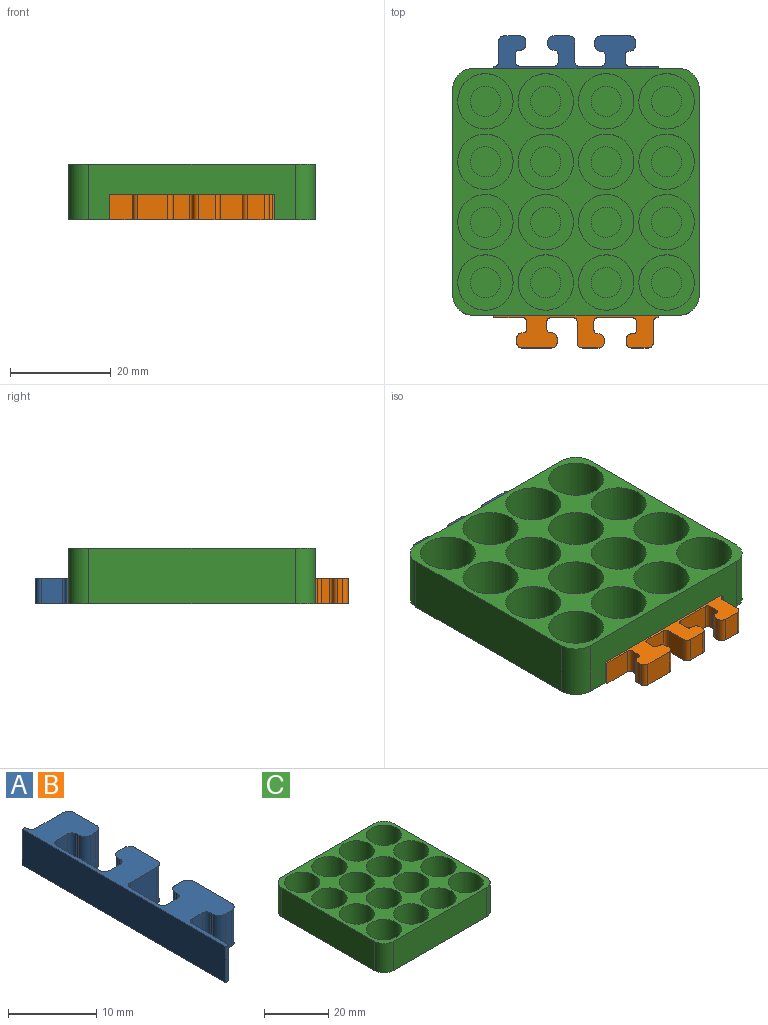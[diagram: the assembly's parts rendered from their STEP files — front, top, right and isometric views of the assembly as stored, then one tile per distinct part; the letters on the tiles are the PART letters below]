
ASSEMBLY  parts=3 mates=2
PART A: 46 faces, bbox 6.5x32.7x5 mm
  f0: plane 5x1.6mm, normal (0,1,0), area 8mm2, adj f24,f25,f38,f39
  f1: plane 5x4.57mm, normal (1,0,0), area 22.9mm2, adj f24,f25,f39,f43
  f2: plane 5x4.3mm, normal (0,-1,0), area 21.5mm2, adj f24,f25,f33,f43
  f3: plane 5x3.37mm, normal (1,0,0), area 16.9mm2, adj f24,f25,f33,f34
  f4: plane 5x0.8mm, normal (0,1,0), area 4mm2, adj f24,f25,f34,f35
  f5: plane 5x0.3mm, normal (-1,0,0), area 1.5mm2, adj f24,f25,f35,f45
  f6: plane 5x1.8mm, normal (0,1,0), area 9mm2, adj f24,f25,f44,f45
  f7: plane 7x5mm, normal (1,0,0), area 35mm2, adj f24,f25,f40,f44
  f8: plane 5x1.8mm, normal (0,-1,0), area 9mm2, adj f24,f25,f40,f41
  f9: plane 5x0.3mm, normal (-1,0,0), area 1.5mm2, adj f24,f25,f30,f41
  f10: plane 5x0.8mm, normal (0,-1,0), area 4mm2, adj f24,f25,f30,f31
  f11: plane 5x3.37mm, normal (1,0,0), area 16.9mm2, adj f24,f25,f31,f32
  f12: plane 5x4.3mm, normal (0,1,0), area 21.5mm2, adj f24,f25,f32,f42
  f13: plane 5x0.3mm, normal (1,0,0), area 1.5mm2, adj f14,f24,f25,f42
  f14: plane 5x0.5mm, normal (0,1,0), area 2.5mm2, adj f13,f15,f24,f25
  f15: plane 32.7x5mm, normal (-1,0,0), area 163.5mm2, adj f14,f16,f24,f25
  f16: plane 5x0.5mm, normal (0,-1,0), area 2.5mm2, adj f15,f17,f24,f25
  f17: plane 5.87x5mm, normal (1,0,0), area 29.4mm2, adj f16,f24,f25,f36
  f18: plane 5x1.6mm, normal (0,-1,0), area 8mm2, adj f24,f25,f36,f37
  f19: plane 5x0.3mm, normal (-1,0,0), area 1.5mm2, adj f24,f25,f26,f37
  f20: plane 5x1mm, normal (0,-1,0), area 5mm2, adj f24,f25,f26,f27
  f21: plane 6x5mm, normal (1,0,0), area 30mm2, adj f24,f25,f27,f28
  f22: plane 5x1mm, normal (0,1,0), area 5mm2, adj f24,f25,f28,f29
  f23: plane 5x0.3mm, normal (-1,0,0), area 1.5mm2, adj f24,f25,f29,f38
  f24: plane 32.7x6.5mm, normal (0,0,1), area 102.9mm2, adj f0,f1,f2,f3,f4,f5,f6,f7
  f25: plane 32.7x6.5mm, normal (0,0,-1), area 102.9mm2, adj f0,f1,f2,f3,f4,f5,f6,f7
  f26: cylinder r=1mm len=5mm, axis (0,0,-1), area 7.9mm2, adj f19,f20,f24,f25
  f27: cylinder r=1mm len=5mm, axis (0,0,-1), area 7.9mm2, adj f20,f21,f24,f25
  f28: cylinder r=1mm len=5mm, axis (0,0,-1), area 7.9mm2, adj f21,f22,f24,f25
  f29: cylinder r=1mm len=5mm, axis (0,0,-1), area 7.9mm2, adj f22,f23,f24,f25
  f30: cylinder r=1mm len=5mm, axis (0,0,-1), area 7.9mm2, adj f9,f10,f24,f25
  f31: cylinder r=1mm len=5mm, axis (0,0,-1), area 7.9mm2, adj f10,f11,f24,f25
  f32: cylinder r=1mm len=5mm, axis (0,0,-1), area 7.9mm2, adj f11,f12,f24,f25
  f33: cylinder r=1mm len=5mm, axis (0,0,-1), area 7.9mm2, adj f2,f3,f24,f25
  f34: cylinder r=1mm len=5mm, axis (0,0,-1), area 7.9mm2, adj f3,f4,f24,f25
  f35: cylinder r=1mm len=5mm, axis (0,0,-1), area 7.9mm2, adj f4,f5,f24,f25
  f36: cylinder r=0.7mm len=5mm, axis (0,0,-1), area 5.5mm2, adj f17,f18,f24,f25
  f37: cylinder r=0.7mm len=5mm, axis (0,0,1), area 5.5mm2, adj f18,f19,f24,f25
  f38: cylinder r=0.7mm len=5mm, axis (0,0,1), area 5.5mm2, adj f0,f23,f24,f25
  f39: cylinder r=0.7mm len=5mm, axis (0,0,-1), area 5.5mm2, adj f0,f1,f24,f25
  f40: cylinder r=0.7mm len=5mm, axis (0,0,-1), area 5.5mm2, adj f7,f8,f24,f25
  f41: cylinder r=0.7mm len=5mm, axis (0,0,1), area 5.5mm2, adj f8,f9,f24,f25
  f42: cylinder r=0.7mm len=5mm, axis (0,0,-1), area 5.5mm2, adj f12,f13,f24,f25
  f43: cylinder r=0.7mm len=5mm, axis (0,0,1), area 5.5mm2, adj f1,f2,f24,f25
  f44: cylinder r=0.7mm len=5mm, axis (0,0,1), area 5.5mm2, adj f6,f7,f24,f25
  f45: cylinder r=0.7mm len=5mm, axis (0,0,1), area 5.5mm2, adj f5,f6,f24,f25
PART B: same geometry as A
PART C: 74 faces, bbox 49x49x11.1 mm
  f0: plane 41x11.1mm, normal (-1,0,0), area 455.1mm2, adj f4,f21,f70,f73
  f1: plane 41x11.1mm, normal (0,-1,0), area 455.1mm2, adj f4,f21,f70,f71
  f2: plane 41x11.1mm, normal (1,0,0), area 455.1mm2, adj f4,f21,f71,f72
  f3: plane 41x11.1mm, normal (0,1,0), area 455.1mm2, adj f4,f21,f72,f73
  f4: plane 49x49mm, normal (0,0,-1), area 2387.3mm2, adj f0,f1,f2,f3,f70,f71,f72,f73
  f5: cylinder r=5.5mm len=11mm, axis (0,0,-1), area 293.7mm2, adj f21,f65
  f6: cylinder r=5.5mm len=11mm, axis (0,0,-1), area 293.7mm2, adj f21,f62
  f7: cylinder r=5.5mm len=11mm, axis (0,0,-1), area 293.7mm2, adj f21,f59
  f8: cylinder r=5.5mm len=11mm, axis (0,0,-1), area 293.7mm2, adj f21,f56
  f9: cylinder r=5.5mm len=11mm, axis (0,0,-1), area 293.7mm2, adj f21,f53
  f10: cylinder r=5.5mm len=11mm, axis (0,0,-1), area 293.7mm2, adj f21,f50
  f11: cylinder r=5.5mm len=11mm, axis (0,0,-1), area 293.7mm2, adj f21,f47
  f12: cylinder r=5.5mm len=11mm, axis (0,0,-1), area 293.7mm2, adj f21,f44
  f13: cylinder r=5.5mm len=11mm, axis (0,0,-1), area 293.7mm2, adj f21,f41
  f14: cylinder r=5.5mm len=11mm, axis (0,0,-1), area 293.7mm2, adj f21,f38
  f15: cylinder r=5.5mm len=11mm, axis (0,0,-1), area 293.7mm2, adj f21,f35
  f16: cylinder r=5.5mm len=11mm, axis (0,0,-1), area 293.7mm2, adj f21,f32
  f17: cylinder r=5.5mm len=11mm, axis (0,0,-1), area 293.7mm2, adj f21,f29
  f18: cylinder r=5.5mm len=11mm, axis (0,0,-1), area 293.7mm2, adj f21,f26
  f19: cylinder r=5.5mm len=11mm, axis (0,0,-1), area 293.7mm2, adj f21,f23
  f20: cylinder r=5.5mm len=11mm, axis (0,0,-1), area 293.7mm2, adj f21,f68
  f21: plane 49x49mm, normal (0,0,1), area 866.7mm2, adj f0,f1,f2,f3,f5,f6,f7,f8
  f22: cylinder r=3mm len=6mm, axis (0,0,-1), area 28.3mm2, adj f23,f24
  f23: plane 11x11mm, normal (0,0,1), area 66.8mm2, adj f19,f22
  f24: plane 6x6mm, normal (0,0,1), area 28.3mm2, adj f22
  f25: cylinder r=3mm len=6mm, axis (0,0,-1), area 28.3mm2, adj f26,f27
  f26: plane 11x11mm, normal (0,0,1), area 66.8mm2, adj f18,f25
  f27: plane 6x6mm, normal (0,0,1), area 28.3mm2, adj f25
  f28: cylinder r=3mm len=6mm, axis (0,0,-1), area 28.3mm2, adj f29,f30
  f29: plane 11x11mm, normal (0,0,1), area 66.8mm2, adj f17,f28
  f30: plane 6x6mm, normal (0,0,1), area 28.3mm2, adj f28
  f31: cylinder r=3mm len=6mm, axis (0,0,-1), area 28.3mm2, adj f32,f33
  f32: plane 11x11mm, normal (0,0,1), area 66.8mm2, adj f16,f31
  f33: plane 6x6mm, normal (0,0,1), area 28.3mm2, adj f31
  f34: cylinder r=3mm len=6mm, axis (0,0,-1), area 28.3mm2, adj f35,f36
  f35: plane 11x11mm, normal (0,0,1), area 66.8mm2, adj f15,f34
  f36: plane 6x6mm, normal (0,0,1), area 28.3mm2, adj f34
  f37: cylinder r=3mm len=6mm, axis (0,0,-1), area 28.3mm2, adj f38,f39
  f38: plane 11x11mm, normal (0,0,1), area 66.8mm2, adj f14,f37
  f39: plane 6x6mm, normal (0,0,1), area 28.3mm2, adj f37
  f40: cylinder r=3mm len=6mm, axis (0,0,-1), area 28.3mm2, adj f41,f42
  f41: plane 11x11mm, normal (0,0,1), area 66.8mm2, adj f13,f40
  f42: plane 6x6mm, normal (0,0,1), area 28.3mm2, adj f40
  f43: cylinder r=3mm len=6mm, axis (0,0,-1), area 28.3mm2, adj f44,f45
  f44: plane 11x11mm, normal (0,0,1), area 66.8mm2, adj f12,f43
  f45: plane 6x6mm, normal (0,0,1), area 28.3mm2, adj f43
  f46: cylinder r=3mm len=6mm, axis (0,0,-1), area 28.3mm2, adj f47,f48
  f47: plane 11x11mm, normal (0,0,1), area 66.8mm2, adj f11,f46
  f48: plane 6x6mm, normal (0,0,1), area 28.3mm2, adj f46
  f49: cylinder r=3mm len=6mm, axis (0,0,-1), area 28.3mm2, adj f50,f51
  f50: plane 11x11mm, normal (0,0,1), area 66.8mm2, adj f10,f49
  f51: plane 6x6mm, normal (0,0,1), area 28.3mm2, adj f49
  f52: cylinder r=3mm len=6mm, axis (0,0,-1), area 28.3mm2, adj f53,f54
  f53: plane 11x11mm, normal (0,0,1), area 66.8mm2, adj f9,f52
  f54: plane 6x6mm, normal (0,0,1), area 28.3mm2, adj f52
  f55: cylinder r=3mm len=6mm, axis (0,0,-1), area 28.3mm2, adj f56,f57
  f56: plane 11x11mm, normal (0,0,1), area 66.8mm2, adj f8,f55
  f57: plane 6x6mm, normal (0,0,1), area 28.3mm2, adj f55
  f58: cylinder r=3mm len=6mm, axis (0,0,-1), area 28.3mm2, adj f59,f60
  f59: plane 11x11mm, normal (0,0,1), area 66.8mm2, adj f7,f58
  f60: plane 6x6mm, normal (0,0,1), area 28.3mm2, adj f58
  f61: cylinder r=3mm len=6mm, axis (0,0,-1), area 28.3mm2, adj f62,f63
  f62: plane 11x11mm, normal (0,0,1), area 66.8mm2, adj f6,f61
  f63: plane 6x6mm, normal (0,0,1), area 28.3mm2, adj f61
  f64: cylinder r=3mm len=6mm, axis (0,0,-1), area 28.3mm2, adj f65,f66
  f65: plane 11x11mm, normal (0,0,1), area 66.8mm2, adj f5,f64
  f66: plane 6x6mm, normal (0,0,1), area 28.3mm2, adj f64
  f67: cylinder r=3mm len=6mm, axis (0,0,-1), area 28.3mm2, adj f68,f69
  f68: plane 11x11mm, normal (0,0,1), area 66.8mm2, adj f20,f67
  f69: plane 6x6mm, normal (0,0,1), area 28.3mm2, adj f67
  f70: cylinder r=4mm len=11.1mm, axis (0,0,-1), area 69.7mm2, adj f0,f1,f4,f21
  f71: cylinder r=4mm len=11.1mm, axis (0,0,1), area 69.7mm2, adj f1,f2,f4,f21
  f72: cylinder r=4mm len=11.1mm, axis (0,0,-1), area 69.7mm2, adj f2,f3,f4,f21
  f73: cylinder r=4mm len=11.1mm, axis (0,0,1), area 69.7mm2, adj f0,f3,f4,f21
PLACE A rot(axis=(0,0,1),90deg) t=(21.05,41.45,1.65)mm
PLACE B rot(axis=(0,0,-1),90deg) t=(21.05,-7.55,1.65)mm
PLACE C t=(-3.45,-7.55,2.75)mm fixed
MATE fastened C.f1 <-> B.f15  axis (0,-1,0) through (21.05,-7.55,1.65)mm
MATE fastened C.f3 <-> A.f15  axis (0,1,0) through (21.05,41.45,1.65)mm
